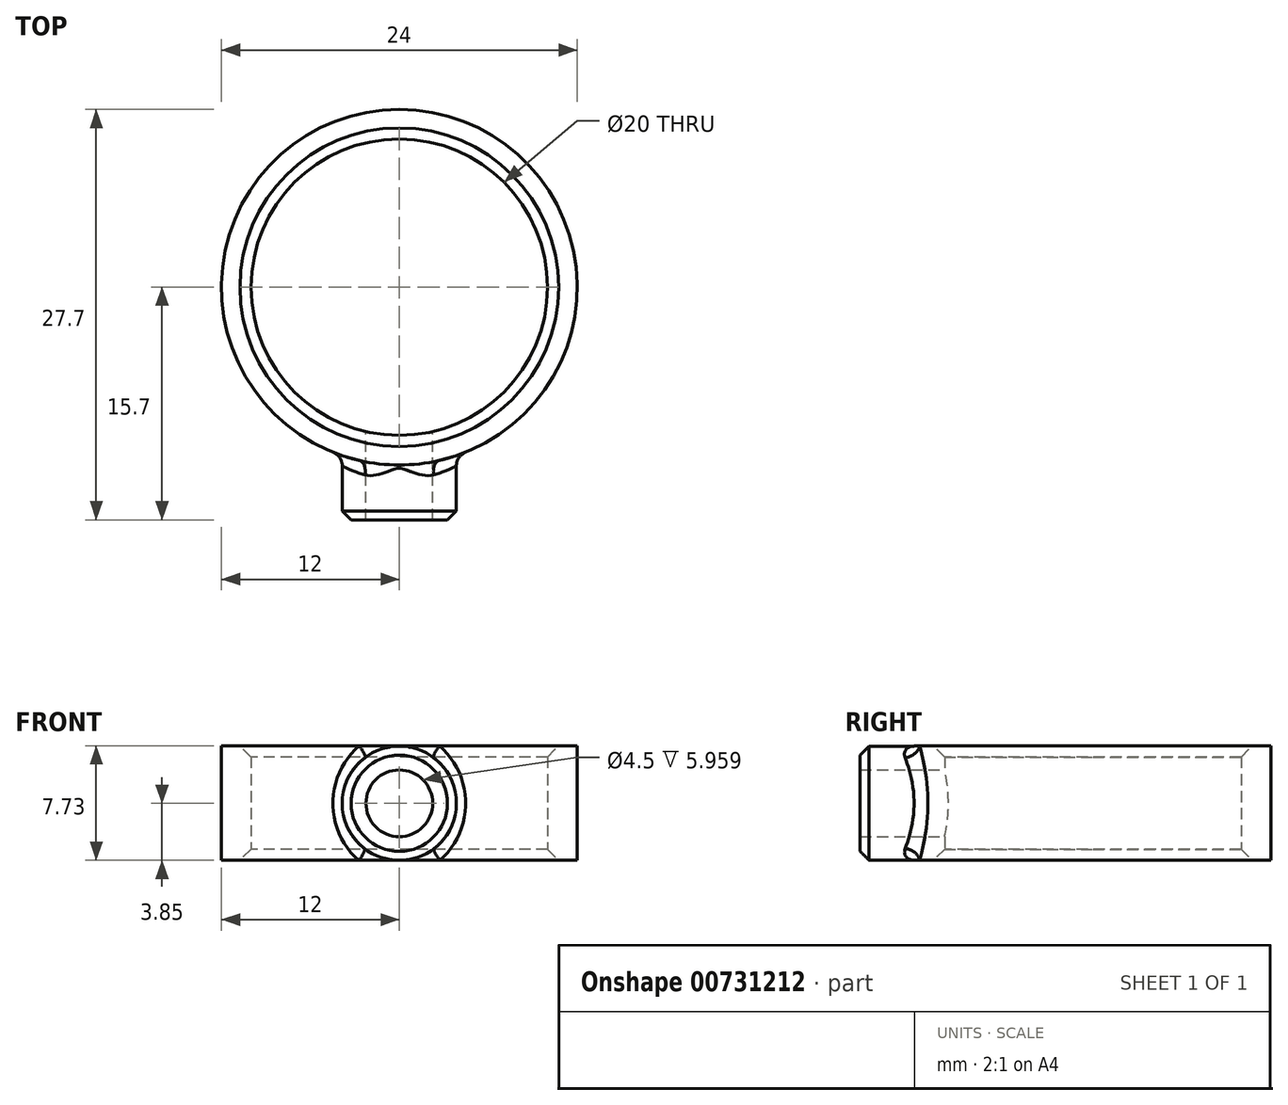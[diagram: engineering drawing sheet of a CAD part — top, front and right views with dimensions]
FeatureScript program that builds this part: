
annotation { "Feature Type Name" : "Feature", "Feature Type Description" : "" }
export const myFeature = defineFeature(function(context is Context, id is Id, definition is map)
    precondition{}
    {
        {
            var Q0;
            Q0=qCreatedBy(makeId("Top.planeOp"),FACE);
            var sketch = newSketch(context, id + "F0", { "sketchPlane" : qUnion([Q0])});
            skCircle(sketch, "E0", {"center": v(0, 0) * mm, "radius": 10 * mm});
            skCircle(sketch, "E1.0", {"center": v(0, 0) * mm, "radius": 12 * mm});
            skSolve(sketch);
        }
        {
            var Q0;
            Q0 = qSketchRegion(id + "F0", true);
            extrude(context, id + "F1", {"entities" : qUnion([Q0]), "depth" : 7.72 * mm, "offsetDistance" : 25 * mm});
        }
        {
            var Q0;
            Q0=qCreatedBy(makeId("Front.planeOp"),FACE);
            cPlane(context, id + "F2", {"entities" : qUnion([Q0]), "cplaneType" : CPlaneType.OFFSET, "offset" : 12 * mm, "width" : 150 * mm, "height" : 150 * mm});
        }
        {
            var Q0;
            Q0=qCreatedBy(id+"F2.planeOp",FACE);
            var sketch = newSketch(context, id + "F3", { "sketchPlane" : qUnion([Q0])});
            skLineSegment(sketch, "E2", {"start": v(0, 0) * mm, "end": v(0, 3.85) * mm});
            skCircle(sketch, "E3", {"center": v(0, 3.85) * mm, "radius": 3.85 * mm});
            skCircle(sketch, "E4", {"center": v(0, 3.85) * mm, "radius": 2.25 * mm});
            skSolve(sketch);
        }
        {
            var Q0;
            Q0 = qSketchRegion(id + "F3", true);
            extrude(context, id + "F4", {"entities" : qUnion([Q0]), "operationType" : NewBodyOperationType.ADD, "depth" : 3.7 * mm, "offsetDistance" : 25 * mm, "hasSecondDirection" : true, "secondDirectionOppositeDirection" : true, "secondDirectionDepth" : 1 * mm});
        }
        {
            var Q0;
            Q0=makeQuery(id+"F4.opExtrude","CAP_EDGE",EDGE,{"disambiguationData":[OSD([sQuery(id+"F3.wireOp",EDGE,"E3")])],"isStart":false});
            chamfer(context, id + "F5", {"entities" : qUnion([Q0]), "width" : .6 * mm, "tangentPropagation" : true});
        }
        {
            var Q0;
            Q0=makeQuery(id+"F1.opExtrude","CAP_EDGE",EDGE,{"disambiguationData":[OSD([sQuery(id+"F0.wireOp",EDGE,"E0")])],"isStart":true});
            var Q1;
            Q1=makeQuery(id+"F1.opExtrude","CAP_EDGE",EDGE,{"disambiguationData":[OSD([sQuery(id+"F0.wireOp",EDGE,"E0")])],"isStart":false});
            chamfer(context, id + "F6", {"entities" : qUnion([Q0, Q1]), "width" : .75 * mm, "tangentPropagation" : true});
        }
        {
            var Q0;
            Q0=qCreatedBy(id+"F2.planeOp",FACE);
            var sketch = newSketch(context, id + "F7", { "sketchPlane" : qUnion([Q0])});
            skLineSegment(sketch, "E5", {"start": v(0, 0) * mm, "end": v(0, 3.85) * mm});
            skCircle(sketch, "E6", {"center": v(0, 3.85) * mm, "radius": 2.25 * mm});
            skSolve(sketch);
        }
        {
            var Q0;
            Q0=makeQuery(id+"F7.imprint","IMPRINT",FACE,{"disambiguationData":[TD([[makeQuery(id+"F7.imprint","IMPRINT",EDGE,{"derivedFrom":sQuery(id+"F7.wireOp",EDGE,"E6")}),1.0]])]});
            extrude(context, id + "F8", {"entities" : qUnion([Q0]), "operationType" : NewBodyOperationType.REMOVE, "oppositeDirection" : true, "depth" : 10 * mm, "offsetDistance" : 25 * mm});
        }
        {
            var Q0;
            Q0=makeQuery(id+"F4.boolean.opBoolean","INTERSECT",EDGE,{"derivedFrom":[makeQuery(id+"F1.opExtrude","SWEPT_FACE",FACE,{"disambiguationData":[OSD([sQuery(id+"F0.wireOp",EDGE,"E1.0")])]}),makeQuery(id+"F4.opExtrude","SWEPT_FACE",FACE,{"disambiguationData":[OSD([sQuery(id+"F3.wireOp",EDGE,"E3")])]})]});
            fillet(context, id + "F9", {"entities" : qUnion([Q0]), "radius" : 1 * mm, "tangentPropagation" : true, "allowEdgeOverflow" : false});
        }
    });
